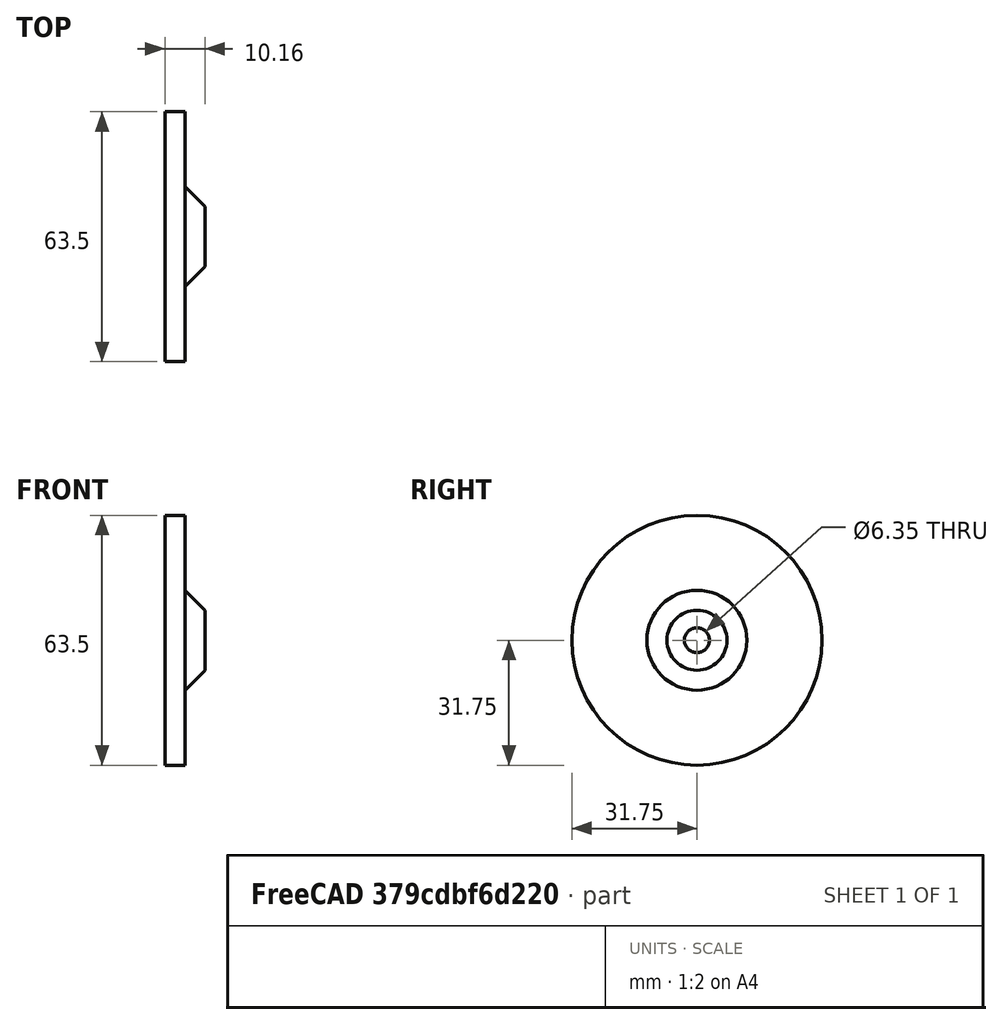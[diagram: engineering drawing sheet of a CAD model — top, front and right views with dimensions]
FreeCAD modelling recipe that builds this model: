
FCSTD DOCUMENT  (FreeCAD 0.19R23578 (Git))
Label: bed_adj_knob
License: All rights reserved
LicenseURL: http://en.wikipedia.org/wiki/All_rights_reserved
objects: Sketcher::SketchObject×1, PartDesign::Revolution×1, PartDesign::Body×1, App::Part×1
note: 4 computed .brp shape members not serialized (recipe doc carries the construction recipe); baked Part::Feature solids carry a one-line shape summary decoded from their .brp

FEATURE [Sketcher::SketchObject] Sketch014
  MapMode = 5
  Placement = pos=(0,0,0) rot=(1,0,0;1.5708rad)
  Support = -> [XZ_Plane001]
  expr: Constraints[12] = 1 / 8 * 25.4
  expr: Constraints[13] = 0.2 * 25.4
  expr: Constraints[14] = 0.2 * 25.4
  expr: Constraints[17] = 0.5 * 25.4
  expr: Constraints[15] = 1.25 * 25.4
  sketch-geometry (6):
    g0: LineSegment StartX=0 StartY=3.175 StartZ=0 EndX=10.16 EndY=3.175 EndZ=0
    g1: LineSegment StartX=10.16 StartY=3.175 StartZ=0 EndX=10.16 EndY=7.62 EndZ=0
    g2: LineSegment StartX=10.16 StartY=7.62 StartZ=0 EndX=5.08 EndY=12.7 EndZ=0
    g3: LineSegment StartX=5.08 StartY=12.7 StartZ=0 EndX=5.08 EndY=31.75 EndZ=0
    g4: LineSegment StartX=5.08 StartY=31.75 StartZ=0 EndX=0 EndY=31.75 EndZ=0
    g5: LineSegment StartX=0 StartY=31.75 StartZ=0 EndX=0 EndY=3.175 EndZ=0
  constraints (18):
    c: Coincident(g0,g1)
    c: Coincident(g1,g2)
    c: Coincident(g2,g3)
    c: Vertical(g3)
    c: Coincident(g3,g4)
    c: Horizontal(g4)
    c: Coincident(g4,g5)
    c: Coincident(g5,g0)
    c: Vertical(g5)
    c: Horizontal(g0)
    c: Vertical(g1)
    c: Angle(g2,g0) = 0.785398
    c: DistanceY(g-1,g0) = 3.175
    c: DistanceX(g4,g4) = 5.08
    c: DistanceX(g2,g1) = 5.08
    c: DistanceY(g-1,g4) = 31.75
    c: PointOnObject(g0,g-2)
    c: DistanceY(g-1,g2) = 12.7
FEATURE [PartDesign::Revolution] Revolution
  AllowMultiFace = false
  Angle = 360
  Axis = (1,0,0)
  Base = (0,0,0)
  Placement = pos=(0,0,0) rot=(1,0,0;1.5708rad)
  Profile = -> Sketch014
  ReferenceAxis = -> X_Axis001
FEATURE [PartDesign::Body] Body007
  Group = -> [Sketch014,Revolution]
  Origin = -> Origin001
  Tip = -> Revolution
FEATURE [App::Part] Part012  label="bed_adj_knob"
  Group = -> [Body007]
  Origin = -> Origin017
  Placement = pos=(1.4e-15,0,0) rot=(0,1,0;1.5708rad)
